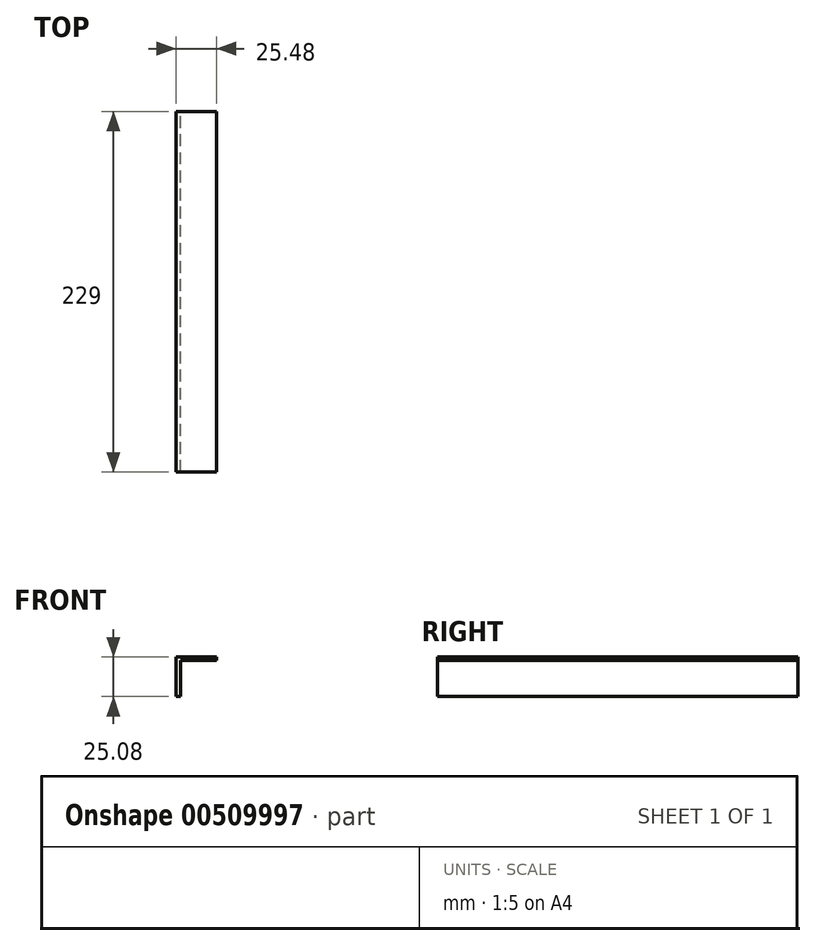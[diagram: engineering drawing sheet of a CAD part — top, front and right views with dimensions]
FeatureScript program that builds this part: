
annotation { "Feature Type Name" : "Feature", "Feature Type Description" : "" }
export const myFeature = defineFeature(function(context is Context, id is Id, definition is map)
    precondition{}
    {
        {
            var Q0;
            Q0=qCreatedBy(makeId("Front.planeOp"),FACE);
            var sketch = newSketch(context, id + "F0", { "sketchPlane" : qUnion([Q0])});
            skLineSegment(sketch, "E0", {"start": v(-12.64, 45.97) * mm, "end": v(-38.12, 45.97) * mm});
            skLineSegment(sketch, "E1", {"start": v(-38.12, 45.97) * mm, "end": v(-38.12, 20.9) * mm});
            skLineSegment(sketch, "E2", {"start": v(-38.12, 20.9) * mm, "end": v(-35.27, 20.9) * mm});
            skLineSegment(sketch, "E3", {"start": v(-35.27, 43.73) * mm, "end": v(-12.64, 43.73) * mm});
            skLineSegment(sketch, "E4", {"start": v(-12.64, 43.73) * mm, "end": v(-12.64, 45.97) * mm});
            skLineSegment(sketch, "E5", {"start": v(-35.27, 43.73) * mm, "end": v(-35.27, 20.9) * mm});
            skSolve(sketch);
        }
        {
            var Q0;
            Q0 = qSketchRegion(id + "F0", true);
            extrude(context, id + "F1", {"entities" : qUnion([Q0]), "depth" : 229 * mm});
        }
    });
